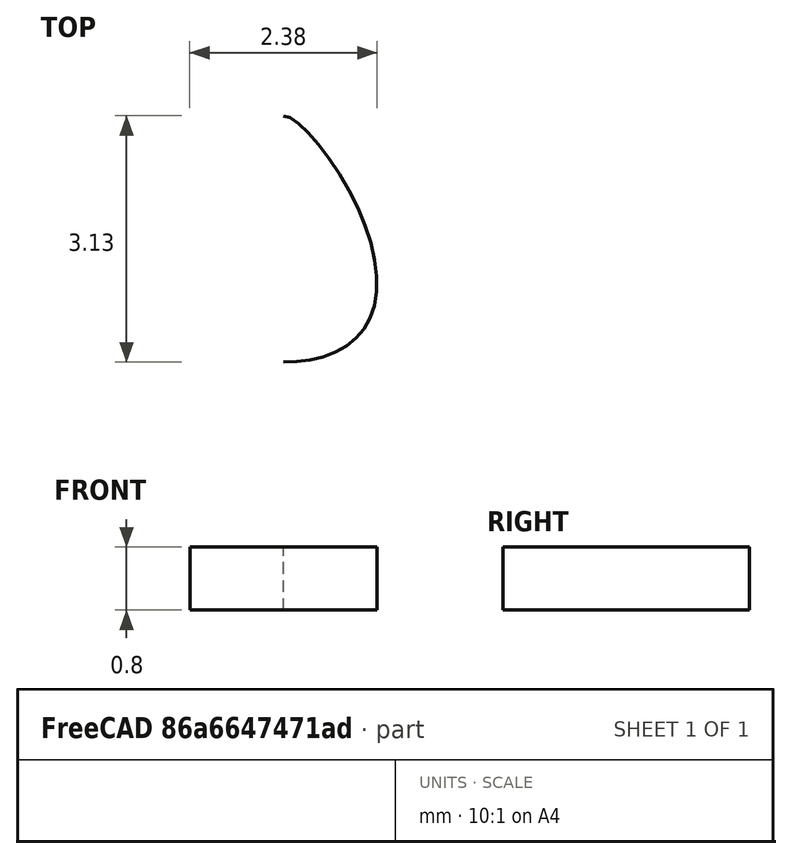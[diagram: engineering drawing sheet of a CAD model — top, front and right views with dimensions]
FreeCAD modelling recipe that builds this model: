
FCSTD DOCUMENT  (FreeCAD 0.17RUnknown)
Label: test117_pick
License: All rights reserved
LicenseURL: http://en.wikipedia.org/wiki/All_rights_reserved
objects: Sketcher::SketchObject×1, PartDesign::Pad×1, PartDesign::Body×1
note: 4 computed .brp shape members not serialized (recipe doc carries the construction recipe); baked Part::Feature solids carry a one-line shape summary decoded from their .brp

FEATURE [Sketcher::SketchObject] Sketch
  MapMode = 5
  Support = -> [XY_Plane]
  sketch-geometry (19):
    g0: LineSegment [constr] StartX=-0.726819 StartY=0.451424 StartZ=0 EndX=0.726819 EndY=0.451424 EndZ=0
    g1: LineSegment [constr] StartX=0.726819 StartY=0.451424 StartZ=0 EndX=0 EndY=2.13973 EndZ=0
    g2: LineSegment [constr] StartX=0 StartY=2.13973 StartZ=0 EndX=-0.726819 EndY=0.451424 EndZ=0
    g3-g6: Circle [constr] x4 (B-spline internal-alignment scaffolding for g7; pole/knot coordinates omitted)
    g7: BSplineCurve PolesCount=5 KnotsCount=2 Degree=4 IsPeriodic=0
    g8: GeomPoint [constr] X=0 Y=3.02829 Z=0
    g9: GeomPoint [constr] X=0 Y=-0.0996766 Z=0
    g10-g13: Circle [constr] x4 (B-spline internal-alignment scaffolding for g14; pole/knot coordinates omitted)
    g14: BSplineCurve PolesCount=5 KnotsCount=2 Degree=4 IsPeriodic=0
    g15: GeomPoint [constr] X=0 Y=3.02829 Z=0
    g16: GeomPoint [constr] X=0 Y=-0.0996766 Z=0
    g17: Circle [constr] CenterX=0 CenterY=-0.0996766 CenterZ=0 NormalX=0 NormalY=0 NormalZ=1 AngleXU=0 Radius=0.07
    g18: Circle [constr] CenterX=0 CenterY=-0.0996766 CenterZ=0 NormalX=0 NormalY=0 NormalZ=1 AngleXU=0 Radius=0.08
  constraints (38):
    c: Coincident(g0,g1)
    c: PointOnObject(g1,g-2)
    c: Coincident(g1,g2)
    c: Coincident(g2,g0)
    c: Symmetric(g0,g0,g-2)
    c: Radius(g3) = 0.07
    c: Equal(g3,g4)
    c: Equal(g3,g5)
    c: Equal(g3,g6)
    c: InternalAlignment(g3-g6 -> g7) x4
    c: InternalAlignment(g8,g7)
    c: InternalAlignment(g9,g7)
    c: PointOnObject(g6,g1)
    c: PointOnObject(g5,g0)
    c: PointOnObject(g4,g2)
    c: PointOnObject(g3,g-2)
    c: Coincident(g10,g3)
    c: Radius(g10) = 0.08
    c: Equal(g10,g11)
    c: Equal(g10,g12)
    c: PointOnObject(g12,g0)
    c: Equal(g10,g13)
    c: PointOnObject(g13,g2)
    c: InternalAlignment(g10-g13 -> g14) x4
    c: InternalAlignment(g15,g14)
    c: InternalAlignment(g16,g14)
    c: Symmetric(g12,g5,g-2)
    c: Symmetric(g11,g4,g-2)
    c: InternalAlignment(g17,g7)
    c: Equal(g17,g3)
    c: InternalAlignment(g18,g14)
    c: Equal(g18,g10)
    c: Coincident(g7,g14)
    c: PointOnObject(g7,g-2)
    c: Symmetric(g13,g6,g-2)
    c: DistanceY(g7,g6) = 0
    c: Distance(g0,g5) = 1.5
    c: Distance(g6,g0) = 0.6
FEATURE [PartDesign::Pad] Pad
  Length = 0.8
  Length2 = 100
  Profile = -> Sketch
  Type = 0
FEATURE [PartDesign::Body] Body
  Group = -> [Sketch,Pad]
  Origin = -> Origin
  Tip = -> Pad
